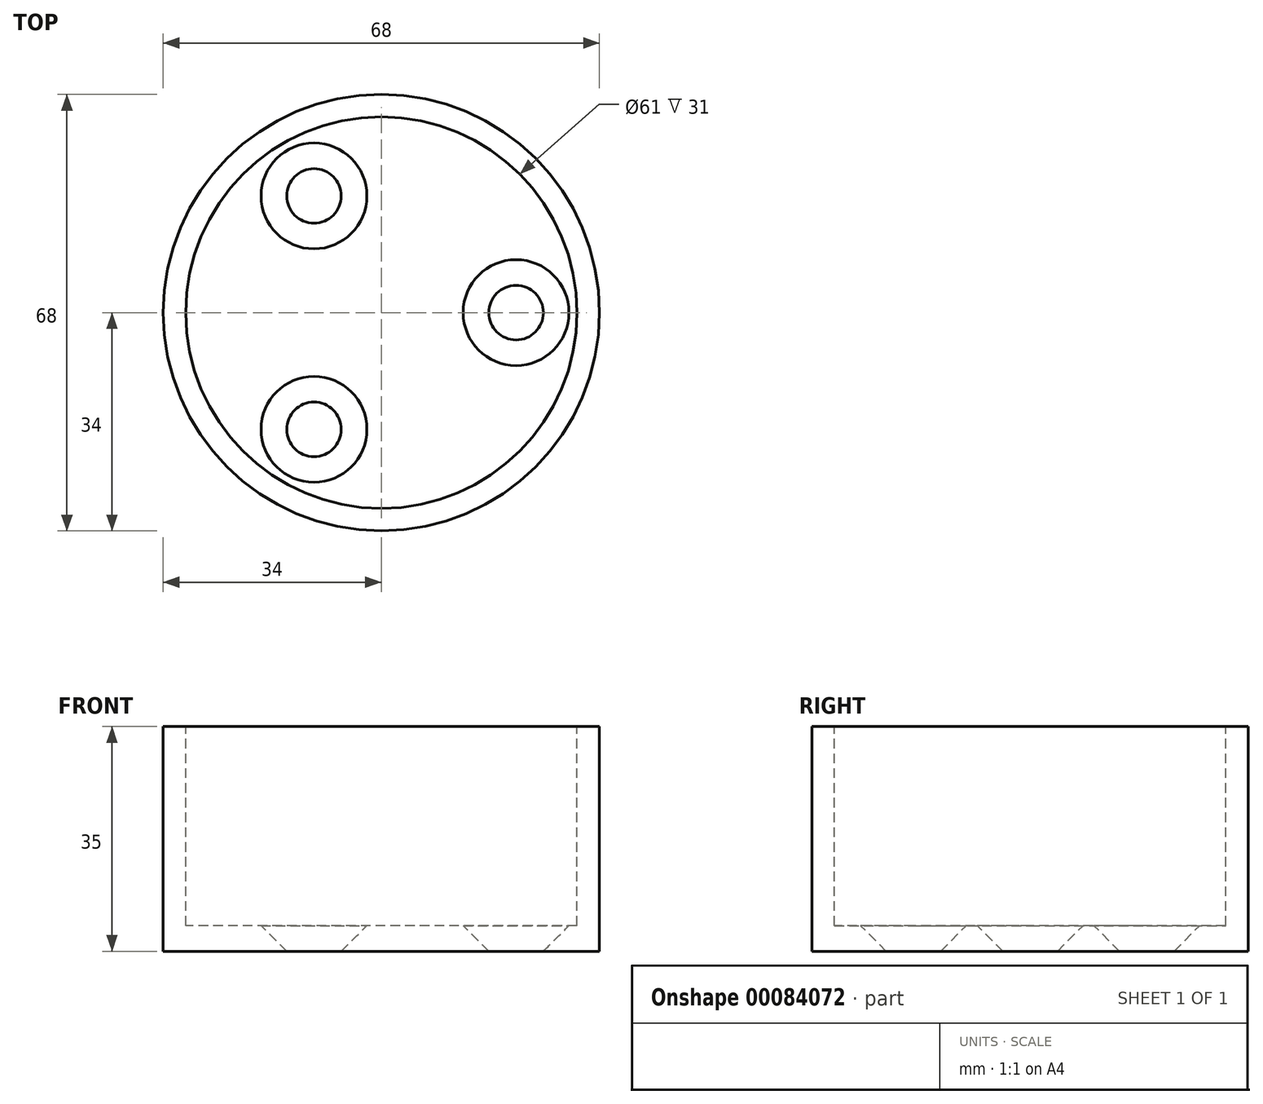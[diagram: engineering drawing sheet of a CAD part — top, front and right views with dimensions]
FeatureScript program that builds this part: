
annotation { "Feature Type Name" : "Feature", "Feature Type Description" : "" }
export const myFeature = defineFeature(function(context is Context, id is Id, definition is map)
    precondition{}
    {
        {
            var Q0;
            Q0=qCreatedBy(makeId("Front.planeOp"),FACE);
            var sketch = newSketch(context, id + "F0", { "sketchPlane" : qUnion([Q0])});
            skLineSegment(sketch, "E0", {"start": v(0, 0) * mm, "end": v(34, 0) * mm});
            skLineSegment(sketch, "E1", {"start": v(34, 0) * mm, "end": v(34, 35) * mm});
            skLineSegment(sketch, "E2", {"start": v(34, 35) * mm, "end": v(30.5, 35) * mm});
            skLineSegment(sketch, "E3", {"start": v(30.5, 35) * mm, "end": v(30.5, 4) * mm});
            skLineSegment(sketch, "E4", {"start": v(30.5, 4) * mm, "end": v(0, 4) * mm});
            skLineSegment(sketch, "E5", {"start": v(0, 4) * mm, "end": v(0, 0) * mm});
            skSolve(sketch);
        }
        {
            var Q0;
            Q0=qCreatedBy(makeId("Top.planeOp"),FACE);
            var sketch = newSketch(context, id + "F1", { "sketchPlane" : qUnion([Q0])});
            skCircle(sketch, "E6", {"center": v(21, 0) * mm, "radius": 4.25 * mm});
            skCircle(sketch, "E7.1.0", {"center": v(-10.5, 18.19) * mm, "radius": 4.25 * mm});
            skCircle(sketch, "E7.2.0", {"center": v(-10.5, -18.19) * mm, "radius": 4.25 * mm});
            skPoint(sketch, "E7.center", {"position": v(0, 0) * mm});
            skSolve(sketch);
        }
        {
            var Q0;
            Q0=makeQuery(id+"F0.imprint","IMPRINT",FACE,{"disambiguationData":[TD([[makeQuery(id+"F0.imprint","IMPRINT",EDGE,{"derivedFrom":sQuery(id+"F0.wireOp",EDGE,"E0")}),1.0]])]});
            var Q1;
            Q1=sQuery(id+"F0.wireOp",EDGE,"E5");
            revolve(context, id + "F2", {"entities" : qUnion([Q0]), "axis" : qUnion([Q1]), "revolveType" : RevolveType.FULL});
        }
        {
            var Q0;
            Q0=makeQuery(id+"F1.imprint","IMPRINT",FACE,{"disambiguationData":[TD([[makeQuery(id+"F1.imprint","IMPRINT",EDGE,{"derivedFrom":sQuery(id+"F1.wireOp",EDGE,"E7.2.0")}),1.0]])]});
            var Q1;
            Q1=makeQuery(id+"F1.imprint","IMPRINT",FACE,{"disambiguationData":[TD([[makeQuery(id+"F1.imprint","IMPRINT",EDGE,{"derivedFrom":sQuery(id+"F1.wireOp",EDGE,"E7.1.0")}),1.0]])]});
            var Q2;
            Q2=makeQuery(id+"F1.imprint","IMPRINT",FACE,{"disambiguationData":[TD([[makeQuery(id+"F1.imprint","IMPRINT",EDGE,{"derivedFrom":sQuery(id+"F1.wireOp",EDGE,"E6")}),1.0]])]});
            extrude(context, id + "F3", {"entities" : qUnion([Q0, Q1, Q2]), "operationType" : NewBodyOperationType.REMOVE, "depth" : 25 * mm});
        }
        {
            var Q0;
            Q0=makeQuery(id+"F3.boolean.opBoolean","INTERSECT",EDGE,{"derivedFrom":[makeQuery(id+"F2.opRevolve","SWEPT_FACE",FACE,{"disambiguationData":[OSD([sQuery(id+"F0.wireOp",EDGE,"E4")])]}),makeQuery(id+"F3.opExtrude","SWEPT_FACE",FACE,{"disambiguationData":[OSD([sQuery(id+"F1.wireOp",EDGE,"E6")])]})]});
            var Q1;
            Q1=makeQuery(id+"F3.boolean.opBoolean","INTERSECT",EDGE,{"derivedFrom":[makeQuery(id+"F2.opRevolve","SWEPT_FACE",FACE,{"disambiguationData":[OSD([sQuery(id+"F0.wireOp",EDGE,"E4")])]}),makeQuery(id+"F3.opExtrude","SWEPT_FACE",FACE,{"disambiguationData":[OSD([sQuery(id+"F1.wireOp",EDGE,"E7.1.0")])]})]});
            var Q2;
            Q2=makeQuery(id+"F3.boolean.opBoolean","INTERSECT",EDGE,{"derivedFrom":[makeQuery(id+"F2.opRevolve","SWEPT_FACE",FACE,{"disambiguationData":[OSD([sQuery(id+"F0.wireOp",EDGE,"E4")])]}),makeQuery(id+"F3.opExtrude","SWEPT_FACE",FACE,{"disambiguationData":[OSD([sQuery(id+"F1.wireOp",EDGE,"E7.2.0")])]})]});
            chamfer(context, id + "F4", {"entities" : qUnion([Q0, Q1, Q2]), "width" : 4 * mm, "tangentPropagation" : true});
        }
    });
